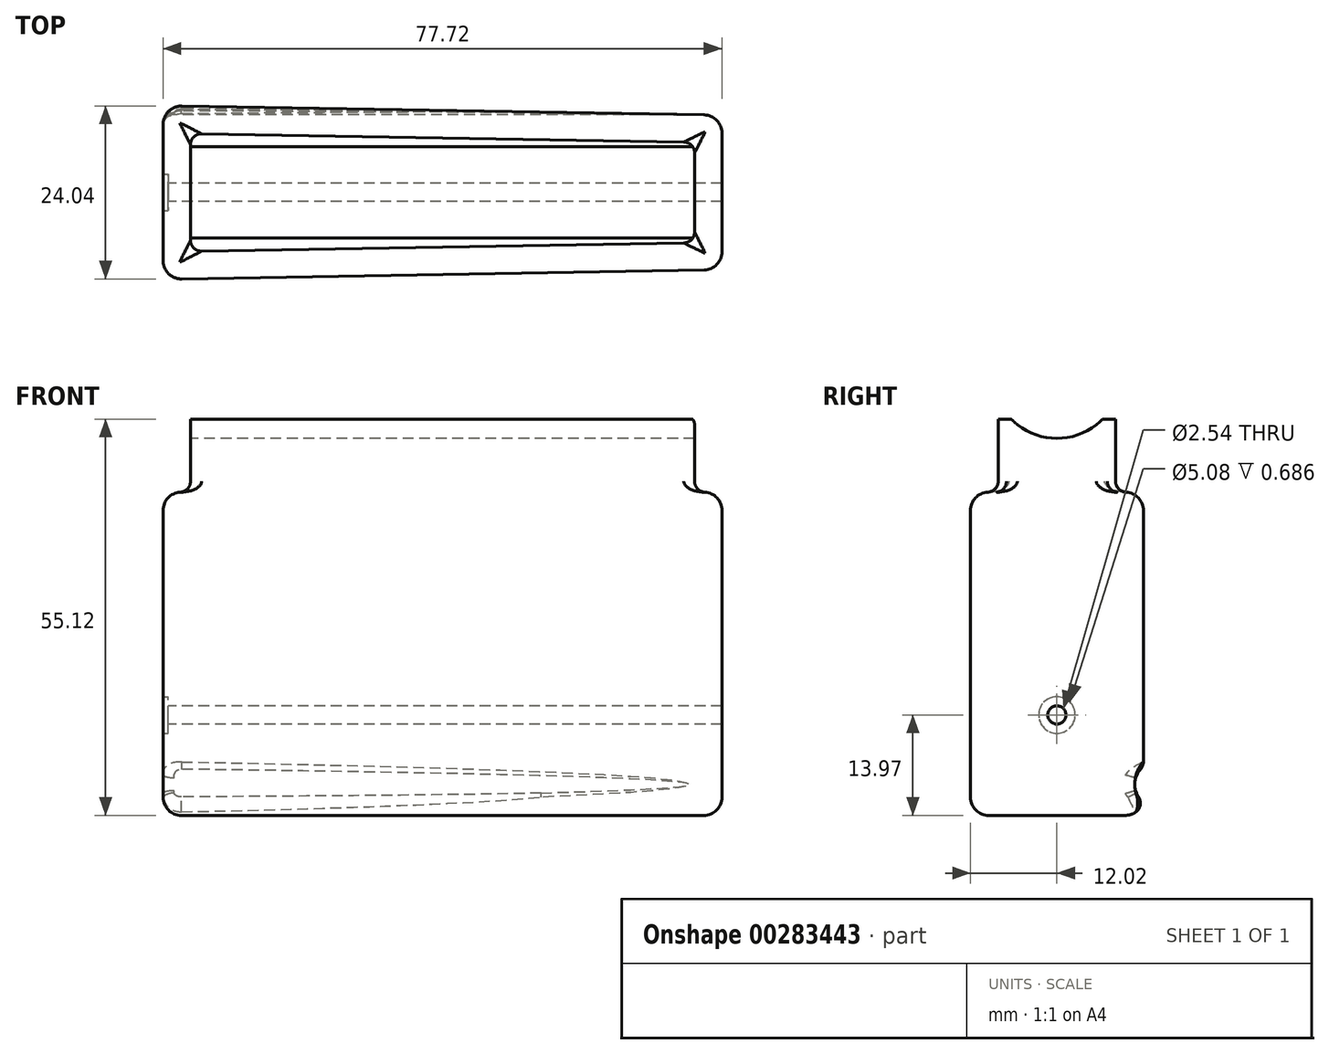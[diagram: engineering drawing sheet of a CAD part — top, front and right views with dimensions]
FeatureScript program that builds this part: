
annotation { "Feature Type Name" : "Feature", "Feature Type Description" : "" }
export const myFeature = defineFeature(function(context is Context, id is Id, definition is map)
    precondition{}
    {
        {
            var Q0;
            Q0=qCreatedBy(makeId("Top.planeOp"),FACE);
            var sketch = newSketch(context, id + "F0", { "sketchPlane" : qUnion([Q0])});
            skLineSegment(sketch, "E0", {"start": v(-38.86, 0) * mm, "end": v(-38.86, 12.07) * mm});
            skLineSegment(sketch, "E1", {"start": v(-38.86, 12.07) * mm, "end": v(38.86, 10.74) * mm});
            skLineSegment(sketch, "E2", {"start": v(38.86, 10.74) * mm, "end": v(38.86, 0) * mm});
            skLineSegment(sketch, "E3", {"start": v(38.86, 0) * mm, "end": v(38.86, -10.74) * mm});
            skLineSegment(sketch, "E4", {"start": v(38.86, -10.74) * mm, "end": v(-38.86, -12.07) * mm});
            skLineSegment(sketch, "E5", {"start": v(-38.86, -12.07) * mm, "end": v(-38.86, 0) * mm});
            skLineSegment(sketch, "E6.0", {"start": v(-35.05, 0) * mm, "end": v(-35.05, 8.19) * mm});
            skLineSegment(sketch, "E6.1", {"start": v(35.05, 7) * mm, "end": v(35.05, 0) * mm});
            skLineSegment(sketch, "E6.2", {"start": v(35.05, 0) * mm, "end": v(35.05, -7) * mm});
            skLineSegment(sketch, "E6.3", {"start": v(-35.05, 8.19) * mm, "end": v(35.05, 7) * mm});
            skLineSegment(sketch, "E6.4", {"start": v(35.05, -7) * mm, "end": v(-35.05, -8.19) * mm});
            skLineSegment(sketch, "E6.5", {"start": v(-35.05, -8.19) * mm, "end": v(-35.05, 0) * mm});
            skSolve(sketch);
        }
        {
            var Q0;
            Q0=qCreatedBy(makeId("Right.planeOp"),FACE);
            var sketch = newSketch(context, id + "F1", { "sketchPlane" : qUnion([Q0])});
            skCircle(sketch, "E7", {"center": v(0, 61.34) * mm, "radius": 8.9 * mm});
            skCircle(sketch, "E8", {"center": v(13.97, 4.32) * mm, "radius": 3.15 * mm});
            skCircle(sketch, "E9.MirrorC", {"center": v(-13.97, 4.32) * mm, "radius": 3.15 * mm});
            skCircle(sketch, "E10", {"center": v(0, 13.97) * mm, "radius": 1.27 * mm});
            skCircle(sketch, "E11", {"center": v(0, 13.97) * mm, "radius": 2.54 * mm});
            skSolve(sketch);
        }
        {
            var Q0;
            Q0=makeQuery(id+"F0.imprint","IMPRINT",FACE,{"disambiguationData":[TD([[makeQuery(id+"F0.imprint","IMPRINT",EDGE,{"derivedFrom":sQuery(id+"F0.wireOp",EDGE,"E6.0")}),-1.0]])]});
            var Q1;
            Q1=makeQuery(id+"F0.imprint","IMPRINT",FACE,{"disambiguationData":[TD([[makeQuery(id+"F0.imprint","IMPRINT",EDGE,{"derivedFrom":sQuery(id+"F0.wireOp",EDGE,"E0")}),-1.0]])]});
            extrude(context, id + "F2", {"entities" : qUnion([Q0, Q1]), "depth" : 44.96 * mm});
        }
        {
            var Q0;
            Q0=makeQuery(id+"F0.imprint","IMPRINT",FACE,{"disambiguationData":[TD([[makeQuery(id+"F0.imprint","IMPRINT",EDGE,{"derivedFrom":sQuery(id+"F0.wireOp",EDGE,"E6.0")}),-1.0]])]});
            extrude(context, id + "F3", {"entities" : qUnion([Q0]), "operationType" : NewBodyOperationType.ADD, "depth" : 55.12 * mm});
        }
        {
            var Q0;
            Q0=makeQuery(id+"F2.opExtrude","SWEPT_FACE",FACE,{"disambiguationData":[OSD([sQuery(id+"F0.wireOp",EDGE,"E1")])]});
            var Q1;
            Q1=makeQuery(id+"F2.opExtrude","SWEPT_FACE",FACE,{"disambiguationData":[OSD([sQuery(id+"F0.wireOp",EDGE,"E0"),sQuery(id+"F0.wireOp",EDGE,"E5")])]});
            var Q2;
            Q2=makeQuery(id+"F2.opExtrude","SWEPT_FACE",FACE,{"disambiguationData":[OSD([sQuery(id+"F0.wireOp",EDGE,"E4")])]});
            var Q3;
            Q3=makeQuery(id+"F2.opExtrude","SWEPT_FACE",FACE,{"disambiguationData":[OSD([sQuery(id+"F0.wireOp",EDGE,"E2"),sQuery(id+"F0.wireOp",EDGE,"E3")])]});
            fillet(context, id + "F4", {"entities" : qUnion([Q0, Q1, Q2, Q3]), "radius" : 2.54 * mm, "tangentPropagation" : true, "allowEdgeOverflow" : false});
        }
        {
            var Q0;
            Q0=makeQuery(id+"F3.boolean.opBoolean","INTERSECT",EDGE,{"derivedFrom":[makeQuery(id+"F2.opExtrude","CAP_FACE",FACE,{"disambiguationData":[OSD([sQuery(id+"F0.wireOp",EDGE,"E0"),sQuery(id+"F0.wireOp",EDGE,"E1"),sQuery(id+"F0.wireOp",EDGE,"E2"),sQuery(id+"F0.wireOp",EDGE,"E3"),sQuery(id+"F0.wireOp",EDGE,"E4"),sQuery(id+"F0.wireOp",EDGE,"E5")])],"isStart":false}),makeQuery(id+"F3.opExtrude","SWEPT_FACE",FACE,{"disambiguationData":[OSD([sQuery(id+"F0.wireOp",EDGE,"E6.0"),sQuery(id+"F0.wireOp",EDGE,"E6.5")])]})]});
            var Q1;
            Q1=makeQuery(id+"F3.boolean.opBoolean","INTERSECT",EDGE,{"derivedFrom":[makeQuery(id+"F2.opExtrude","CAP_FACE",FACE,{"disambiguationData":[OSD([sQuery(id+"F0.wireOp",EDGE,"E0"),sQuery(id+"F0.wireOp",EDGE,"E1"),sQuery(id+"F0.wireOp",EDGE,"E2"),sQuery(id+"F0.wireOp",EDGE,"E3"),sQuery(id+"F0.wireOp",EDGE,"E4"),sQuery(id+"F0.wireOp",EDGE,"E5")])],"isStart":false}),makeQuery(id+"F3.opExtrude","SWEPT_FACE",FACE,{"disambiguationData":[OSD([sQuery(id+"F0.wireOp",EDGE,"E6.3")])]})]});
            var Q2;
            Q2=makeQuery(id+"F3.boolean.opBoolean","INTERSECT",EDGE,{"derivedFrom":[makeQuery(id+"F2.opExtrude","CAP_FACE",FACE,{"disambiguationData":[OSD([sQuery(id+"F0.wireOp",EDGE,"E0"),sQuery(id+"F0.wireOp",EDGE,"E1"),sQuery(id+"F0.wireOp",EDGE,"E2"),sQuery(id+"F0.wireOp",EDGE,"E3"),sQuery(id+"F0.wireOp",EDGE,"E4"),sQuery(id+"F0.wireOp",EDGE,"E5")])],"isStart":false}),makeQuery(id+"F3.opExtrude","SWEPT_FACE",FACE,{"disambiguationData":[OSD([sQuery(id+"F0.wireOp",EDGE,"E6.1"),sQuery(id+"F0.wireOp",EDGE,"E6.2")])]})]});
            var Q3;
            Q3=makeQuery(id+"F3.boolean.opBoolean","INTERSECT",EDGE,{"derivedFrom":[makeQuery(id+"F2.opExtrude","CAP_FACE",FACE,{"disambiguationData":[OSD([sQuery(id+"F0.wireOp",EDGE,"E0"),sQuery(id+"F0.wireOp",EDGE,"E1"),sQuery(id+"F0.wireOp",EDGE,"E2"),sQuery(id+"F0.wireOp",EDGE,"E3"),sQuery(id+"F0.wireOp",EDGE,"E4"),sQuery(id+"F0.wireOp",EDGE,"E5")])],"isStart":false}),makeQuery(id+"F3.opExtrude","SWEPT_FACE",FACE,{"disambiguationData":[OSD([sQuery(id+"F0.wireOp",EDGE,"E6.4")])]})]});
            fillet(context, id + "F5", {"entities" : qUnion([Q0, Q1, Q2, Q3]), "radius" : 1.52 * mm, "tangentPropagation" : true, "allowEdgeOverflow" : false});
        }
        {
            var Q0;
            Q0=makeQuery(id+"F1.imprint","IMPRINT",FACE,{"disambiguationData":[TD([[makeQuery(id+"F1.imprint","IMPRINT",EDGE,{"derivedFrom":sQuery(id+"F1.wireOp",EDGE,"E7")}),1.0]])]});
            var Q1;
            Q1=makeQuery(id+"F1.imprint","IMPRINT",FACE,{"disambiguationData":[TD([[makeQuery(id+"F1.imprint","IMPRINT",EDGE,{"derivedFrom":sQuery(id+"F1.wireOp",EDGE,"E8")}),1.0]])]});
            var Q2;
            Q2=makeQuery(id+"F1.imprint","IMPRINT",FACE,{"disambiguationData":[TD([[makeQuery(id+"F1.imprint","IMPRINT",EDGE,{"derivedFrom":sQuery(id+"F1.wireOp",EDGE,"E9.MirrorC")}),-1.0]])]});
            var Q3;
            Q3=makeQuery(id+"F1.imprint","IMPRINT",FACE,{"disambiguationData":[TD([[makeQuery(id+"F1.imprint","IMPRINT",EDGE,{"derivedFrom":sQuery(id+"F1.wireOp",EDGE,"E10")}),1.0]])]});
            extrude(context, id + "F6", {"entities" : qUnion([Q0, Q1, Q2, Q3]), "operationType" : NewBodyOperationType.REMOVE, "depth" : 101.6 * mm, "symmetric" : true});
        }
        {
            var Q0;
            Q0=makeQuery(id+"F1.imprint","IMPRINT",FACE,{"disambiguationData":[TD([[makeQuery(id+"F1.imprint","IMPRINT",EDGE,{"derivedFrom":sQuery(id+"F1.wireOp",EDGE,"E10")}),-1.0]])]});
            extrude(context, id + "F7", {"entities" : qUnion([Q0]), "operationType" : NewBodyOperationType.REMOVE, "oppositeDirection" : true, "depth" : 53.1 * mm, "hasSecondDirection" : true, "secondDirectionOppositeDirection" : true, "secondDirectionDepth" : 38.18 * mm});
        }
        {
            var Q0;
            Q0=makeQuery(id+"F6.boolean.opBoolean","COPY",FACE,{"derivedFrom":makeQuery(id+"F6.opExtrude","SWEPT_FACE",FACE,{"disambiguationData":[OSD([sQuery(id+"F1.wireOp",EDGE,"E8")])]})});
            var Q1;
            Q1=makeQuery(id+"F6.boolean.opBoolean","COPY",FACE,{"derivedFrom":makeQuery(id+"F6.opExtrude","SWEPT_FACE",FACE,{"disambiguationData":[OSD([sQuery(id+"F1.wireOp",EDGE,"E9.MirrorC")])]})});
            var Q2;
            Q2=makeQuery(id+"F3.opExtrude","SWEPT_EDGE",EDGE,{"disambiguationData":[OSD([sQuery(id+"F0.wireOp",EDGE,"E6.0"),sQuery(id+"F0.wireOp",EDGE,"E6.3")])]});
            var Q3;
            Q3=makeQuery(id+"F3.opExtrude","SWEPT_EDGE",EDGE,{"disambiguationData":[OSD([sQuery(id+"F0.wireOp",EDGE,"E6.4"),sQuery(id+"F0.wireOp",EDGE,"E6.5")])]});
            var Q4;
            Q4=makeQuery(id+"F3.opExtrude","SWEPT_EDGE",EDGE,{"disambiguationData":[OSD([sQuery(id+"F0.wireOp",EDGE,"E6.1"),sQuery(id+"F0.wireOp",EDGE,"E6.3")])]});
            var Q5;
            Q5=makeQuery(id+"F3.opExtrude","SWEPT_EDGE",EDGE,{"disambiguationData":[OSD([sQuery(id+"F0.wireOp",EDGE,"E6.2"),sQuery(id+"F0.wireOp",EDGE,"E6.4")])]});
            fillet(context, id + "F8", {"entities" : qUnion([Q0, Q1, Q2, Q3, Q4, Q5]), "radius" : 1.52 * mm, "tangentPropagation" : true, "allowEdgeOverflow" : false});
        }
    });
